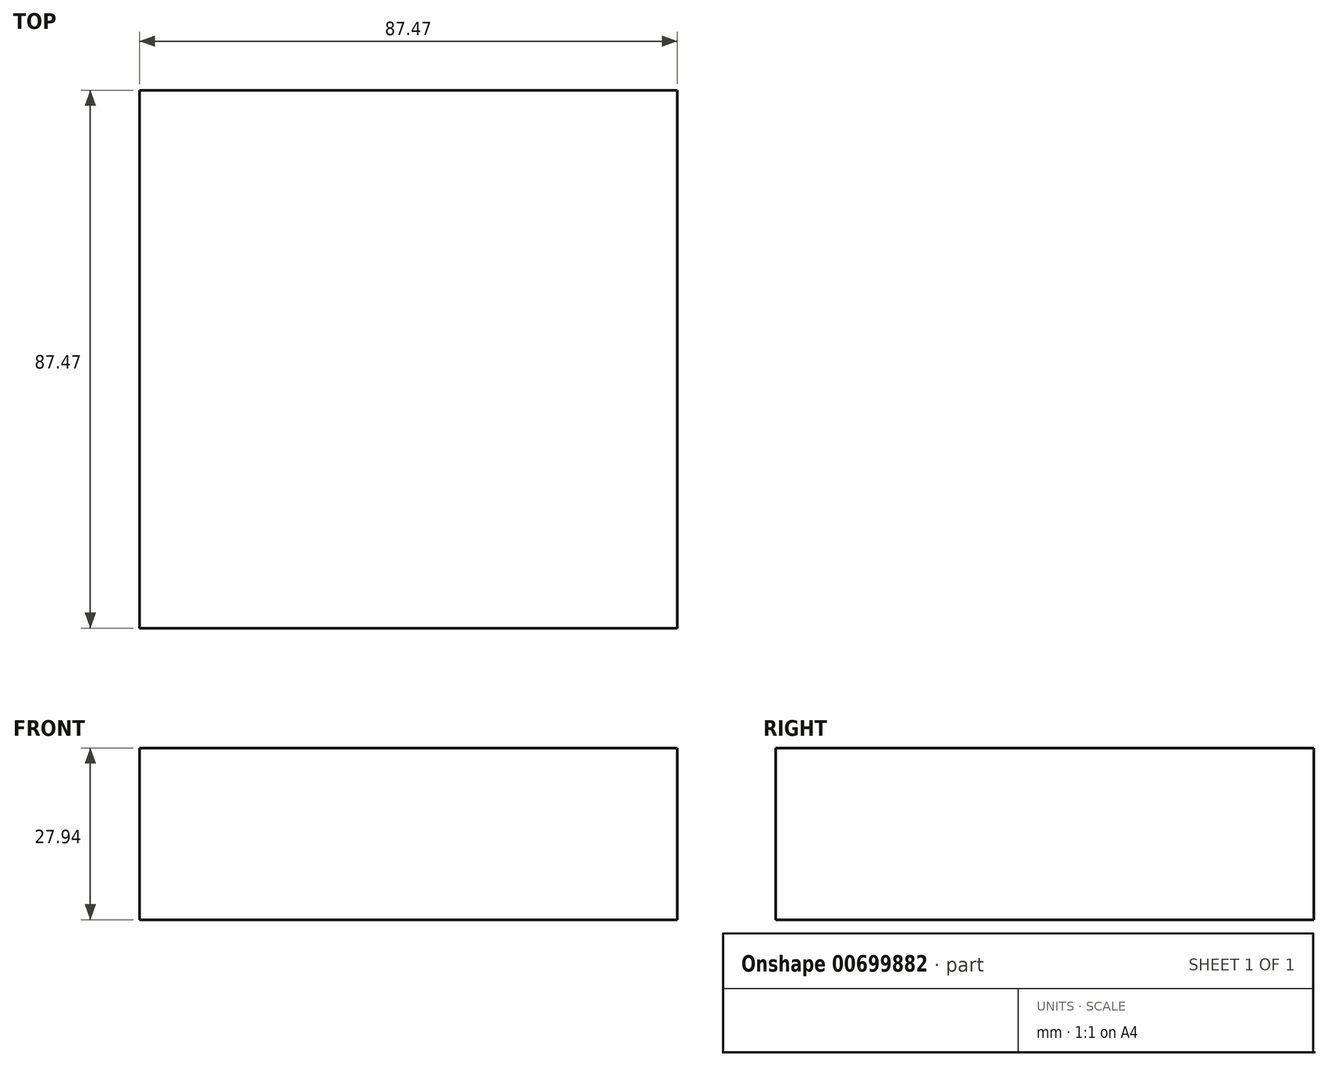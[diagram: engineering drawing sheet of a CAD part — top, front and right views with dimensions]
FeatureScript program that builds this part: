
annotation { "Feature Type Name" : "Feature", "Feature Type Description" : "" }
export const myFeature = defineFeature(function(context is Context, id is Id, definition is map)
    precondition{}
    {
        {
            var Q0;
            Q0=qCreatedBy(makeId("Top.planeOp"),FACE);
            var sketch = newSketch(context, id + "F0", { "sketchPlane" : qUnion([Q0])});
            skLineSegment(sketch, "E0", {"start": v(-76.88, 39.7) * mm, "end": v(10.6, 39.7) * mm});
            skLineSegment(sketch, "E1", {"start": v(10.6, 39.7) * mm, "end": v(10.6, -47.77) * mm});
            skLineSegment(sketch, "E2", {"start": v(10.6, -47.77) * mm, "end": v(-76.88, -47.77) * mm});
            skLineSegment(sketch, "E3", {"start": v(-76.88, -47.77) * mm, "end": v(-76.88, 39.7) * mm});
            skSolve(sketch);
        }
        {
            var Q0;
            Q0=makeQuery(id+"F0.imprint","IMPRINT",FACE,{"disambiguationData":[TD([[makeQuery(id+"F0.imprint","IMPRINT",EDGE,{"derivedFrom":sQuery(id+"F0.wireOp",EDGE,"E0")}),-1.0]])]});
            extrude(context, id + "F1", {"entities" : qUnion([Q0]), "depth" : 27.94 * mm, "offsetDistance" : 25.4 * mm});
        }
    });
